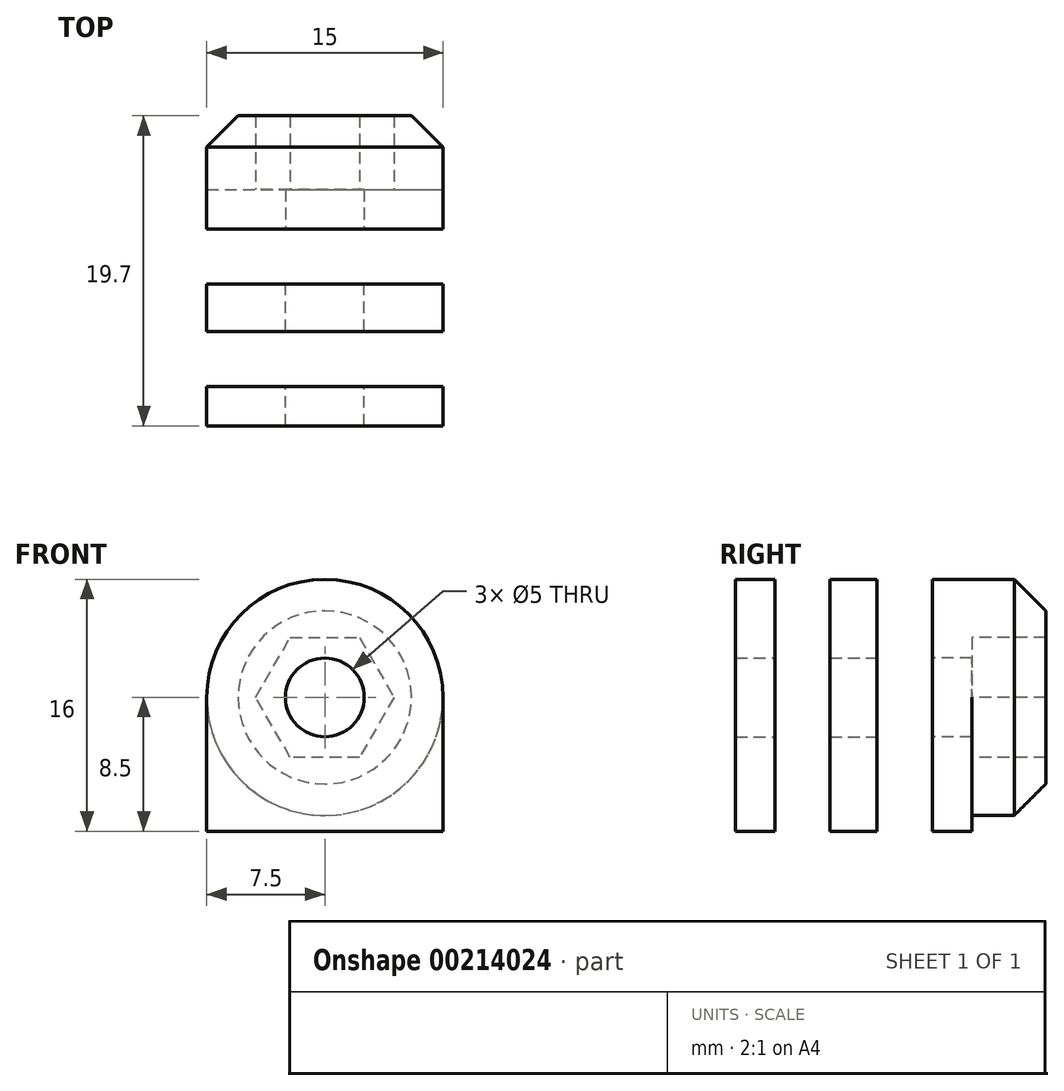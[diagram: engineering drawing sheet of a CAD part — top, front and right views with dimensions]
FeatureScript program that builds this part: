
annotation { "Feature Type Name" : "Feature", "Feature Type Description" : "" }
export const myFeature = defineFeature(function(context is Context, id is Id, definition is map)
    precondition{}
    {
        {
            var Q0;
            Q0=qCreatedBy(makeId("Front.planeOp"),FACE);
            var sketch = newSketch(context, id + "F0", { "sketchPlane" : qUnion([Q0])});
            skCircle(sketch, "E0", {"center": v(0, 0) * mm, "radius": 2.5 * mm});
            skCircle(sketch, "E1", {"center": v(0, 0) * mm, "radius": 7.5 * mm});
            skLineSegment(sketch, "E2", {"start": v(-7.5, 0) * mm, "end": v(-7.5, -8.5) * mm});
            skLineSegment(sketch, "E3", {"start": v(-7.5, -8.5) * mm, "end": v(7.5, -8.5) * mm});
            skLineSegment(sketch, "E4", {"start": v(7.5, 0) * mm, "end": v(7.5, -8.5) * mm});
            skCircle(sketch, "E5.cCircle", {"center": v(0, 0) * mm, "radius": 3.8 * mm, "construction": true});
            skLineSegment(sketch, "E5.0", {"start": v(4.4, 0) * mm, "end": v(2.2, -3.8) * mm});
            skLineSegment(sketch, "E5.1", {"start": v(2.2, -3.8) * mm, "end": v(-2.2, -3.8) * mm});
            skLineSegment(sketch, "E5.2", {"start": v(-2.2, -3.8) * mm, "end": v(-4.4, 0) * mm});
            skLineSegment(sketch, "E5.3", {"start": v(-4.4, 0) * mm, "end": v(-2.2, 3.8) * mm});
            skLineSegment(sketch, "E5.4", {"start": v(-2.2, 3.8) * mm, "end": v(2.2, 3.8) * mm});
            skLineSegment(sketch, "E5.5", {"start": v(2.2, 3.8) * mm, "end": v(4.4, 0) * mm});
            skPoint(sketch, "E5.0.midPoint", {"position": v(3.3, -1.9) * mm});
            skSolve(sketch);
        }
        {
            var Q0;
            {var subQ0=sQuery(id+"F0.wireOp",EDGE,"E2");Q0=makeQuery(id+"F0.imprint","IMPRINT",FACE,{"disambiguationData":[TD([[makeQuery(id+"F0.imprint","IMPRINT",EDGE,{"derivedFrom":subQ0}),1.0]])]});}
            var Q1;
            Q1=makeQuery(id+"F0.imprint","IMPRINT",FACE,{"disambiguationData":[TD([[makeQuery(id+"F0.imprint","IMPRINT",EDGE,{"derivedFrom":sQuery(id+"F0.wireOp",EDGE,"E5.0")}),1.0]])]});
            var Q2;
            Q2=makeQuery(id+"F0.imprint","IMPRINT",FACE,{"disambiguationData":[TD([[makeQuery(id+"F0.imprint","IMPRINT",EDGE,{"derivedFrom":sQuery(id+"F0.wireOp",EDGE,"E0")}),-1.0]])]});
            extrude(context, id + "F1", {"entities" : qUnion([Q0, Q1, Q2]), "endBound" : BoundingType.SYMMETRIC, "depth" : 3 * mm});
        }
        {
            var Q0;
            {var subQ0=sQuery(id+"F0.wireOp",EDGE,"E2");Q0=makeQuery(id+"F0.imprint","IMPRINT",FACE,{"disambiguationData":[TD([[makeQuery(id+"F0.imprint","IMPRINT",EDGE,{"derivedFrom":subQ0}),1.0]])]});}
            var Q1;
            Q1=makeQuery(id+"F0.imprint","IMPRINT",FACE,{"disambiguationData":[TD([[makeQuery(id+"F0.imprint","IMPRINT",EDGE,{"derivedFrom":sQuery(id+"F0.wireOp",EDGE,"E5.0")}),1.0]])]});
            var Q2;
            Q2=makeQuery(id+"F0.imprint","IMPRINT",FACE,{"disambiguationData":[TD([[makeQuery(id+"F0.imprint","IMPRINT",EDGE,{"derivedFrom":sQuery(id+"F0.wireOp",EDGE,"E0")}),-1.0]])]});
            extrude(context, id + "F2", {"entities" : qUnion([Q0, Q1, Q2]), "depth" : 7.5 * mm, "hasSecondDirection" : true, "secondDirectionOppositeDirection" : false, "secondDirectionDepth" : 5 * mm});
        }
        {
            var Q0;
            Q0=makeQuery(id+"F0.imprint","IMPRINT",FACE,{"disambiguationData":[TD([[makeQuery(id+"F0.imprint","IMPRINT",EDGE,{"derivedFrom":sQuery(id+"F0.wireOp",EDGE,"E5.0")}),1.0]])]});
            var Q1;
            {var subQ0=sQuery(id+"F0.wireOp",EDGE,"E2");Q1=makeQuery(id+"F0.imprint","IMPRINT",FACE,{"disambiguationData":[TD([[makeQuery(id+"F0.imprint","IMPRINT",EDGE,{"derivedFrom":subQ0}),1.0]])]});}
            var Q2;
            Q2=makeQuery(id+"F0.imprint","IMPRINT",FACE,{"disambiguationData":[TD([[makeQuery(id+"F0.imprint","IMPRINT",EDGE,{"derivedFrom":sQuery(id+"F0.wireOp",EDGE,"E0")}),-1.0]])]});
            extrude(context, id + "F3", {"entities" : qUnion([Q0, Q1, Q2]), "oppositeDirection" : true, "depth" : 7.5 * mm, "hasSecondDirection" : true, "secondDirectionOppositeDirection" : true, "secondDirectionDepth" : 5 * mm});
        }
        {
            var Q0;
            Q0=makeQuery(id+"F0.imprint","IMPRINT",FACE,{"disambiguationData":[TD([[makeQuery(id+"F0.imprint","IMPRINT",EDGE,{"derivedFrom":sQuery(id+"F0.wireOp",EDGE,"E5.0")}),1.0]])]});
            extrude(context, id + "F4", {"entities" : qUnion([Q0]), "operationType" : NewBodyOperationType.ADD, "oppositeDirection" : true, "depth" : 12.2 * mm, "hasSecondDirection" : true, "secondDirectionOppositeDirection" : true, "secondDirectionDepth" : 7.5 * mm});
        }
        {
            var Q0;
            Q0=makeQuery(id+"F4.opExtrude","CAP_EDGE",EDGE,{"disambiguationData":[OSD([sQuery(id+"F0.wireOp",EDGE,"E1")])],"isStart":false});
            chamfer(context, id + "F5", {"entities" : qUnion([Q0]), "width" : 2 * mm, "tangentPropagation" : true});
        }
    });
